# Revit family: NAU_Naughtone_Stng_Viv_Stools1
name_source: partatom
category: Furniture
revit_build: Autodesk Revit 2018 (Build: 20170223_1515(x64)
units: mm (PartAtom-declared; Revit-internal decimal feet)

## family parameters
Always vertical = Yes
Cut with Voids When Loaded = No
OmniClass Number = 23.40.20.00
OmniClass Title = General Furniture and Specialties
Room Calculation Point = No
Shared = Yes
Work Plane-Based = No

## types (4) — shared parameters
Assembly Code = E2020200
AssetType = Movable
BIMObjectName = NAU_Naughtone_Seating_Viv_Stools
Category = Pr_40_50_12 : Chairs, seats and benches
Color = Various
DurationUnit = year
Finish = Fabric Upholstery
IfcExportAs = IfcFurnishingElementType
IfcExportType = STOOL
Keynote = Pr_40_50_12_85
MainColor = Various
ManufacturerAddress = Knaresborough Tech Park, Manse Lane, Knaresborough, HG5 8LF
ManufacturerName = Naughtone
ManufacturerURL = www.naughtone.com
Material = Fabric, Foam, Polypropylene, Steel
NBSDescription = Seating
NBSReference = 45-35-72/352
Name = Seating_Viv_Stools_Naughtone
ProductInformation = www.naughtone.com/products/viv/
Revision = 1
Shape = Rectangular
SustainabilityPerformance = FSC certified. FISP certified. ISO 14001
URL = www.naughtone.com
Uniclass2015Code = Pr_40_50_12_85
Uniclass2015Title = Stools
Version = 1
WarrantyDescription = Request warranty information from naughtone
WarrantyDurationLabor = 7
WarrantyDurationParts = 7
WarrantyDurationUnit = year

## per-type parameters (varying)
| type | Description | IsVIVBSB4L | IsVIVBSSL | IsVIVCHSB4L | IsVIVCHSSL | Model | ModelNumber | ModelReference | NominalHeight | NominalLength | NominalWidth | Size |
| Viv Counter Height Stool with Sled Base_VIVCHSSL | Viv Counter Height Stool with Sled Base | No | No | No | Yes | VIVCHSSL | VIVCHSSL | Viv Counter Height Stool with Sled Base | 915 mm  [stored 3.00197 ft] | 565 mm  [stored 1.85367 ft] | 545 mm  [stored 1.78806 ft] | 565 x 545 x 915 mm |
| Viv Barstool with Sled Base_VIVBSSL | Viv Barstool with Sled Base | No | Yes | No | No | VIVBSSL | VIVBSSL | Viv Barstool with Sled Base | 1025 mm  [stored 3.36286 ft] | 565 mm  [stored 1.85367 ft] | 575 mm | 565 x 575 x 1025 mm |
| Viv Counter Height Stool with 4 Leg Base_VIVCHSB4L | Viv Counter Height Stool with 4 Leg Base | No | No | Yes | No | VIVCHSB4L | VIVCHSB4L | Viv Counter Height Stool with 4 Leg Base | 955 mm  [stored 3.1332 ft] | 570 mm  [stored 1.87008 ft] | 535 mm  [stored 1.75525 ft] | 570 x 535 x 995 mm |
| Viv Barstool with 4 Leg Base_VIVBSB4L | Viv Barstool with 4 Leg Base | Yes | No | No | No | VIVBSB4L | VIVBSB4L | Viv Barstool with 4 Leg Base | 1055 mm  [stored 3.46129 ft] | 570 mm  [stored 1.87008 ft] | 535 mm  [stored 1.75525 ft] | 570 x 535 x 1055 mm |

note: [stored X ft] marks values corroborated as IEEE doubles in the binary element streams (Revit-internal decimal feet)

## geometry (parser evidence)
native form markers: Sweep x5
no freeform markers — native parametric forms only
